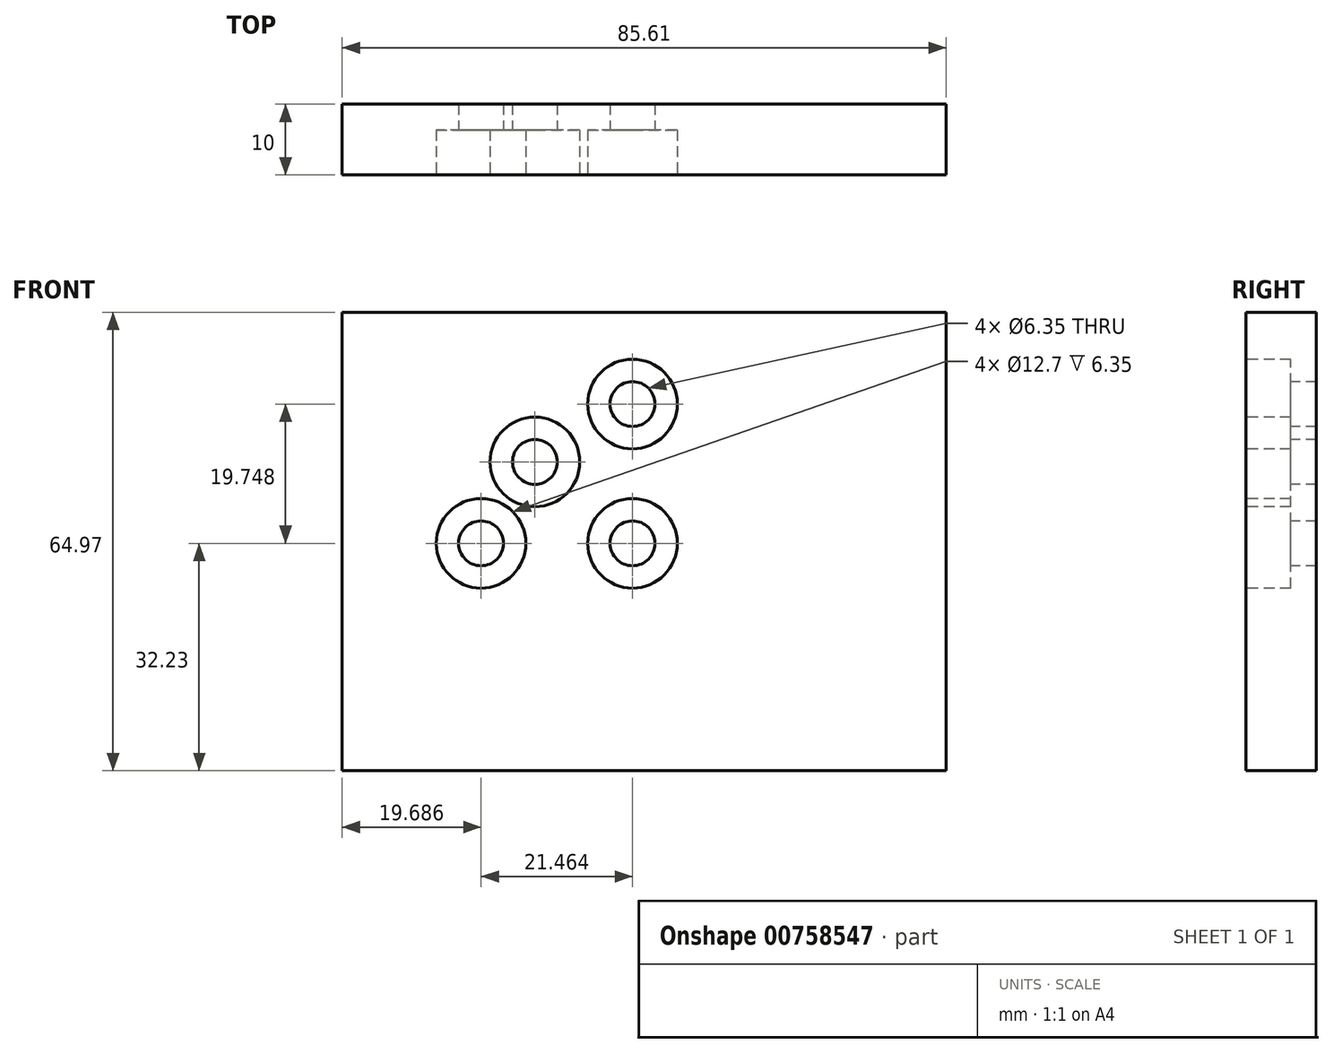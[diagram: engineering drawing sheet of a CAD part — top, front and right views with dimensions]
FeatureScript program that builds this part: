
annotation { "Feature Type Name" : "Feature", "Feature Type Description" : "" }
export const myFeature = defineFeature(function(context is Context, id is Id, definition is map)
    precondition{}
    {
        {
            var Q0;
            Q0=qCreatedBy(makeId("Front.planeOp"),FACE);
            var sketch = newSketch(context, id + "F0", { "sketchPlane" : qUnion([Q0])});
            skLineSegment(sketch, "E0.bottom", {"start": v(-41.15, -32.23) * mm, "end": v(44.46, -32.23) * mm});
            skLineSegment(sketch, "E0.top", {"start": v(-41.15, 32.74) * mm, "end": v(44.46, 32.74) * mm});
            skLineSegment(sketch, "E0.left", {"start": v(-41.15, -32.23) * mm, "end": v(-41.15, 32.74) * mm});
            skLineSegment(sketch, "E0.right", {"start": v(44.46, -32.23) * mm, "end": v(44.46, 32.74) * mm});
            skPoint(sketch, "E1", {"position": v(0, 0) * mm});
            skPoint(sketch, "E2", {"position": v(-25.4, 0) * mm});
            skSolve(sketch);
        }
        {
            var Q0;
            Q0 = qSketchRegion(id + "F0", true);
            extrude(context, id + "F1", {"entities" : qUnion([Q0]), "depth" : 10 * mm, "offsetDistance" : 25.4 * mm});
        }
        {
            var Q0;
            Q0=makeQuery(id+"F1.opExtrude","CAP_FACE",FACE,{"disambiguationData":[OSD([sQuery(id+"F0.wireOp",EDGE,"E0.bottom"),sQuery(id+"F0.wireOp",EDGE,"E0.top"),sQuery(id+"F0.wireOp",EDGE,"E0.left"),sQuery(id+"F0.wireOp",EDGE,"E0.right")])],"isStart":false});
            var sketch = newSketch(context, id + "F2", { "sketchPlane" : qUnion([Q0])});
            skPoint(sketch, "E3", {"position": v(0, 0) * mm});
            skPoint(sketch, "E4", {"position": v(-21.46, 0) * mm});
            skPoint(sketch, "E5", {"position": v(0, 19.75) * mm});
            skPoint(sketch, "E6", {"position": v(0, -17.7) * mm});
            skPoint(sketch, "E7", {"position": v(17.57, 11.54) * mm});
            skPoint(sketch, "E8", {"position": v(17.57, -10.9) * mm});
            skPoint(sketch, "E9", {"position": v(-13.83, -9.51) * mm});
            skPoint(sketch, "E10", {"position": v(-13.83, 11.54) * mm});
            skPoint(sketch, "E11", {"position": v(0, 10.12) * mm});
            skPoint(sketch, "E12", {"position": v(0, -9.33) * mm});
            skSolve(sketch);
        }
        {
            var Q0;
            Q0=sQuery(id+"F2.wireOp",VERTEX,"E3");
            var Q1;
            Q1=sQuery(id+"F2.wireOp",VERTEX,"E4");
            var Q2;
            Q2=sQuery(id+"F2.wireOp",VERTEX,"E10");
            var Q3;
            Q3=sQuery(id+"F2.wireOp",VERTEX,"E5");
            var Q4;
            Q4=makeQuery(id+"F1.opExtrude","SWEPT_BODY",BODY,{"disambiguationData":[OSD([sQuery(id+"F0.wireOp",EDGE,"E0.bottom"),sQuery(id+"F0.wireOp",EDGE,"E0.top"),sQuery(id+"F0.wireOp",EDGE,"E0.left"),sQuery(id+"F0.wireOp",EDGE,"E0.right")])]});
            hole(context, id + "F3", {"style" : HoleStyle.C_BORE, "endStyle" : HoleEndStyle.THROUGH, "holeDiameter" : 6.35 * mm, "cBoreDiameter" : 12.7 * mm, "cBoreDepth" : 6.35 * mm, "majorDiameter" : 6.35 * mm, "isTappedThrough" : true, "tappedDepth" : 12.7 * mm, "tapClearance" : 3, "locations" : qUnion([Q0, Q1, Q2, Q3]), "scope" : qUnion([Q4])});
        }
    });
